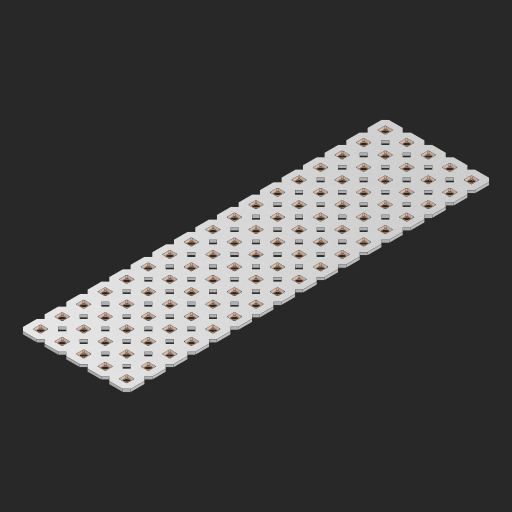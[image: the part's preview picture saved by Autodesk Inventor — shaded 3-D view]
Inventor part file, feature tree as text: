
AUTODESK INVENTOR PART (.ipt)
format: ipt  version: 2023 (Build 270158000, 158)  size: 1,270,272 bytes
history: native  units: in
note: dims shown in document units (in); Inventor stores cm internally (conversion verified against a paired STEP export)
features: other x86, extrude x84, sketch x2, pattern_linear x1
ambient origin geometry x8: Origin, YZ Plane, XZ Plane, XY Plane, X Axis, Y Axis, Z Axis, Center Point
bodies: Solid1 (feature_tree), Body (feature_tree)
feature tree (173):
  pattern_linear  "Rectangular Pattern1"  Spacing1=0.09in  [1 undecoded]
  sketch  "Sketch1"  dims[d1=0.5in]
  sketch  "Sketch2"  dims[d2=0.182in d3=0.09in d4=0.09in d5=0.09in d6=0.09in d7=0.09in d8=0.09in d9=0.09in d10=0.09in d11=0.02in d13=0.0in d14=0.172in d15=0.0625in d16=0.0in d19=0.5in d22=0.5in]
  other  "Srf1"
  other  "Srf126"
  other  "Srf127"
  other  "Srf128"
  other  "Srf129"
  other  "Srf130"
  other  "Srf131"
  other  "Srf250"
  other  "Srf251"
  other  "Srf252"
  other  "Srf253"
  other  "Srf254"
  other  "Srf255"
  other  "Srf256"
  other  "Srf257"
  other  "Srf258"
  other  "Srf259"
  other  "Srf268"
  other  "Srf269"
  other  "Srf270"
  other  "Srf271"
  other  "Srf272"
  other  "Srf273"
  other  "Srf274"
  other  "Srf275"
  other  "Srf276"
  other  "Srf277"
  other  "Srf278"
  other  "Srf279"
  other  "Srf280"
  other  "Srf281"
  other  "Srf282"
  other  "Srf283"
  other  "Srf284"
  other  "Srf293"
  other  "Srf294"
  other  "Srf295"
  other  "Srf296"
  other  "Srf297"
  other  "Srf298"
  other  "Srf299"
  other  "Srf300"
  other  "Srf301"
  other  "Srf302"
  other  "Srf303"
  other  "Srf304"
  other  "Srf305"
  other  "Srf306"
  other  "Srf307"
  other  "Srf308"
  other  "Srf309"
  other  "Srf318"
  other  "Srf319"
  other  "Srf320"
  other  "Srf321"
  other  "Srf322"
  other  "Srf323"
  other  "Srf324"
  other  "Srf325"
  other  "Srf326"
  other  "Srf327"
  other  "Srf328"
  other  "Srf329"
  other  "Srf330"
  other  "Srf331"
  other  "Srf332"
  other  "Srf333"
  other  "Srf334"
  other  "Srf343"
  other  "Srf344"
  other  "Srf345"
  other  "Srf346"
  other  "Srf347"
  other  "Srf348"
  other  "Srf349"
  other  "Srf350"
  other  "Srf351"
  other  "Srf352"
  other  "Srf353"
  other  "Srf354"
  other  "Srf355"
  other  "Srf356"
  other  "Srf357"
  other  "Srf358"
  other  "Srf359"
  other  "Circle"
  extrude  "ExtrusionSrf126"  Depth=0.09in
  extrude  "ExtrusionSrf127"  Depth=0.09in
  extrude  "ExtrusionSrf128"  Depth=0.09in
  extrude  "ExtrusionSrf129"  Depth=0.09in
  extrude  "ExtrusionSrf130"  Depth=0.09in
  extrude  "ExtrusionSrf131"  Depth=0.09in
  extrude  "ExtrusionSrf250"  Depth=0.09in
  extrude  "ExtrusionSrf251"  Depth=0.02in
  extrude  "ExtrusionSrf252"  TaperAngle=0.0deg  [1 undecoded]
  extrude  "ExtrusionSrf253"  Depth=0.5in
  extrude  "ExtrusionSrf254"  Depth=0.0625in TaperAngle=0.0deg
  extrude  "ExtrusionSrf255"  Depth=0.5in
  extrude  "ExtrusionSrf256"  Depth=0.5in
  extrude  "ExtrusionSrf257"  [1 undecoded]
  extrude  "ExtrusionSrf258"  [1 undecoded]
  extrude  "ExtrusionSrf259"  [1 undecoded]
  extrude  "ExtrusionSrf268"  [1 undecoded]
  extrude  "ExtrusionSrf269"  [1 undecoded]
  extrude  "ExtrusionSrf270"  [1 undecoded]
  extrude  "ExtrusionSrf271"  [1 undecoded]
  extrude  "ExtrusionSrf272"  [1 undecoded]
  extrude  "ExtrusionSrf273"  [1 undecoded]
  extrude  "ExtrusionSrf274"  [1 undecoded]
  extrude  "ExtrusionSrf275"  [1 undecoded]
  extrude  "ExtrusionSrf276"  [1 undecoded]
  extrude  "ExtrusionSrf277"  [1 undecoded]
  extrude  "ExtrusionSrf278"  [1 undecoded]
  extrude  "ExtrusionSrf279"  [1 undecoded]
  extrude  "ExtrusionSrf280"  [1 undecoded]
  extrude  "ExtrusionSrf281"  [1 undecoded]
  extrude  "ExtrusionSrf282"  [1 undecoded]
  extrude  "ExtrusionSrf283"  [1 undecoded]
  extrude  "ExtrusionSrf284"  [1 undecoded]
  extrude  "ExtrusionSrf293"  [1 undecoded]
  extrude  "ExtrusionSrf294"  [1 undecoded]
  extrude  "ExtrusionSrf295"  [1 undecoded]
  extrude  "ExtrusionSrf296"  [1 undecoded]
  extrude  "ExtrusionSrf297"  [1 undecoded]
  extrude  "ExtrusionSrf298"  [1 undecoded]
  extrude  "ExtrusionSrf299"  [1 undecoded]
  extrude  "ExtrusionSrf300"  [1 undecoded]
  extrude  "ExtrusionSrf301"  [1 undecoded]
  extrude  "ExtrusionSrf302"  [1 undecoded]
  extrude  "ExtrusionSrf303"  [1 undecoded]
  extrude  "ExtrusionSrf304"  [1 undecoded]
  extrude  "ExtrusionSrf305"  [1 undecoded]
  extrude  "ExtrusionSrf306"  [1 undecoded]
  extrude  "ExtrusionSrf307"  [1 undecoded]
  extrude  "ExtrusionSrf308"  [1 undecoded]
  extrude  "ExtrusionSrf309"  [1 undecoded]
  extrude  "ExtrusionSrf318"  [1 undecoded]
  extrude  "ExtrusionSrf319"  [1 undecoded]
  extrude  "ExtrusionSrf320"  [1 undecoded]
  extrude  "ExtrusionSrf321"  [1 undecoded]
  extrude  "ExtrusionSrf322"  [1 undecoded]
  extrude  "ExtrusionSrf323"  [1 undecoded]
  extrude  "ExtrusionSrf324"  [1 undecoded]
  extrude  "ExtrusionSrf325"  [1 undecoded]
  extrude  "ExtrusionSrf326"  [1 undecoded]
  extrude  "ExtrusionSrf327"  [1 undecoded]
  extrude  "ExtrusionSrf328"  [1 undecoded]
  extrude  "ExtrusionSrf329"  [1 undecoded]
  extrude  "ExtrusionSrf330"  [1 undecoded]
  extrude  "ExtrusionSrf331"  [1 undecoded]
  extrude  "ExtrusionSrf332"  [1 undecoded]
  extrude  "ExtrusionSrf333"  [1 undecoded]
  extrude  "ExtrusionSrf334"  [1 undecoded]
  extrude  "ExtrusionSrf343"  [1 undecoded]
  extrude  "ExtrusionSrf344"  [1 undecoded]
  extrude  "ExtrusionSrf345"  [1 undecoded]
  extrude  "ExtrusionSrf346"  [1 undecoded]
  extrude  "ExtrusionSrf347"  [1 undecoded]
  extrude  "ExtrusionSrf348"  [1 undecoded]
  extrude  "ExtrusionSrf349"  [1 undecoded]
  extrude  "ExtrusionSrf350"  [1 undecoded]
  extrude  "ExtrusionSrf351"  [1 undecoded]
  extrude  "ExtrusionSrf352"  [1 undecoded]
  extrude  "ExtrusionSrf353"  [1 undecoded]
  extrude  "ExtrusionSrf354"  [1 undecoded]
  extrude  "ExtrusionSrf355"  [1 undecoded]
  extrude  "ExtrusionSrf356"  [1 undecoded]
  extrude  "ExtrusionSrf357"  [1 undecoded]
  extrude  "ExtrusionSrf358"  [1 undecoded]
  extrude  "ExtrusionSrf359"  [1 undecoded]
note: 73 required parameter values undecoded (feature->parameter linkage not recoverable at this tier; creation-order binding heuristic only, values carry confidence <= 0.55)
